# Revit family: BE_31094_en_GB
name_source: partatom
category: Leuchten
units: mm (PartAtom-declared; Revit-internal decimal feet)

## family parameters
Basisbauteil = Fläche
Beim Laden mit Abzugskörper schneiden = Ja
Bemaßung runder Anschluss = Durchmesser verwenden
Gemeinsam genutzt = Nein
Lichtquelle = Ja
Raumberechnungspunkt = Ja
Teiletyp = Normal

## types (1)
- BEGA_31094_K3
    AC/DC = AC/DC
    Ambient_temperature = 25 °C
    BEGA_dummy = Nein
    BEGA_internal = Ja
    BEGA_internal_off = Ja
    BEGA_internal_on = Ja
    BEGA_internal_structure = Ja
    Bega_IES = Ja
    Beschreibung = Wall luminaire
    CE_conformity = yes
    Colour_rendering_index = CRI > 80
    Colour_temperature = 3000 K
    Custom_made_product = Nein
    Datei für fotometrisches Netz = BE_31094K3.IES
    Description_custom_made_product = Here you can specify modifications of your custom-made product
    ENEC = yes
    Energy_efficiency_class = LED A++ - A
    Farbfilter = 16777215
    Farbtemperaturverschiebung bei Dämpfen der Lampe = <Keine Auswahl>
    Fixing_distance = 52 mm
    Fixing_hole = Ø 4,5 mm
    Frequency = 0/50-60 Hz
    Hersteller = BEGA
    LED_module_designation = LED-0317/830
    Lamp_luminous_flux = 590 lm
    Lampe = LED 2.9 W
    Load_Classification = Lighting
    Logo = BEGA_Logo.png
    Luminaire_luminous_flux = 383 lm
    M_A = Nein
    M_G = Nein
    M_W = Nein
    Material_02 = BEGA_finishes_silver_matt
    Material_03 = BEGA_finishes_white_matt
    Material_06 = BEGA_finishes_stainless_steel_brushed
    Material_09 = BEGA_glass_clear
    Material_11 = BEGA_glass_opal
    Material_15 = BEGA_lighting_medium_matt
    Material_17 = BEGA_reflector
    Material_18 = BEGA_rubber_black
    Material_28 = BEGA_finishes_copper_matt
    Material_31 = BEGA_finishes_brass_matt
    Modell = 31094K3
    Neigungswinkel = 0,00°
    Order_number = 31094K3
    Product_data_sheet = https://cdn.bega.com
    Protection_class = IP 44
    Safety_class = I
    Scheinlast = 0 VA
    Service_life_criteria = L70B50 @ 25 °C = 200000 h
    URL = https://www.bega.com
    Update = 2022-05-18T04:00:13
    Voltage = 240 V
    Vorgabe-Ansicht = 0 mm  [stored 0 ft]
    Weight = 2.0 kg

note: [stored X ft] marks values corroborated as IEEE doubles in the binary element streams (Revit-internal decimal feet)

## geometry (parser evidence)
native form markers: Sweep x2
no freeform markers — native parametric forms only
